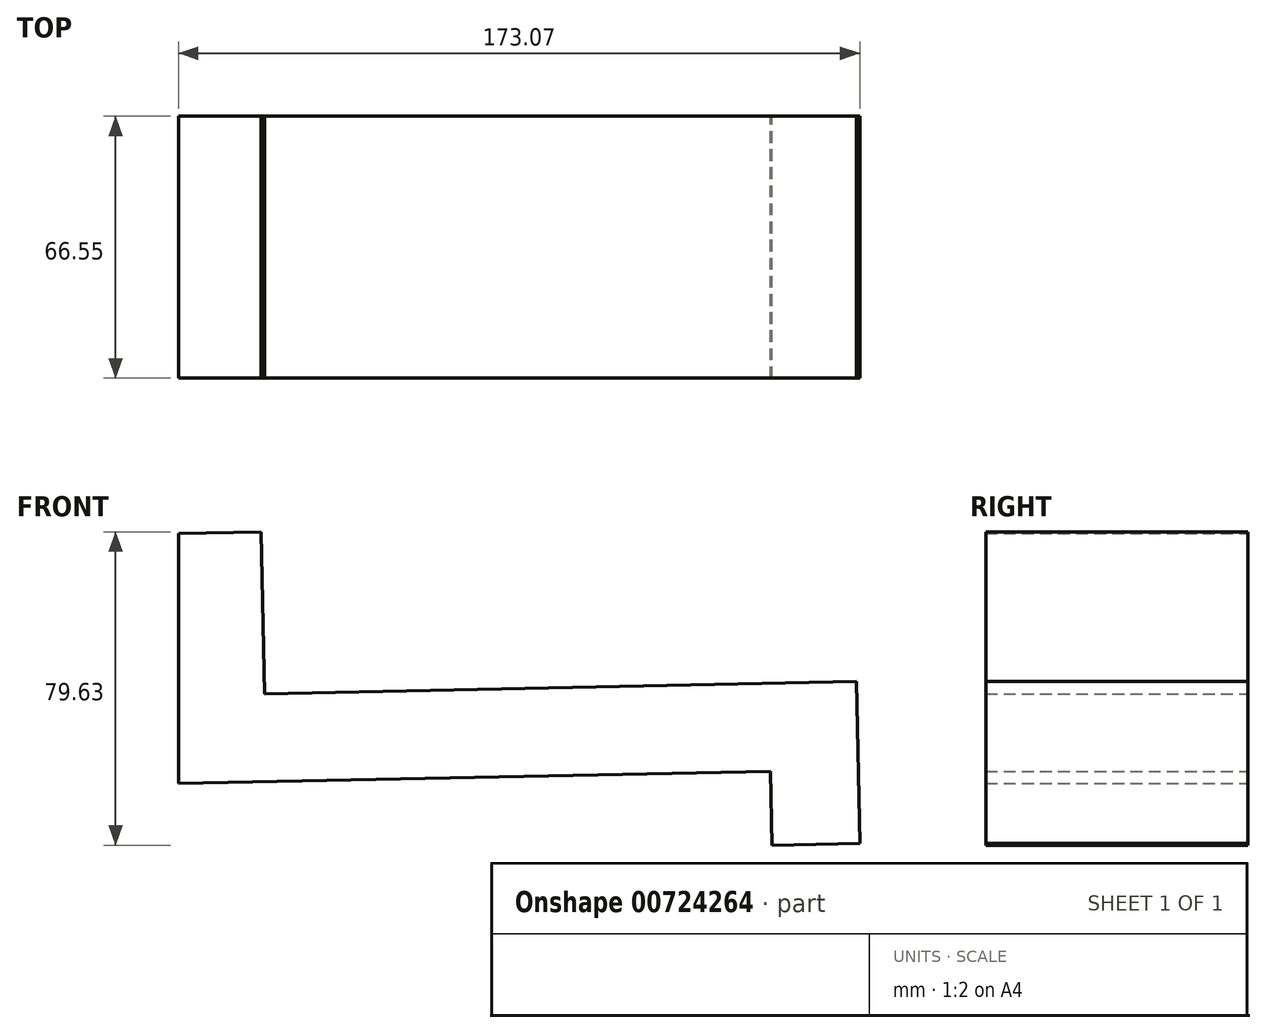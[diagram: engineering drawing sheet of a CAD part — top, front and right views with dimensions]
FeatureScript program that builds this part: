
annotation { "Feature Type Name" : "Feature", "Feature Type Description" : "" }
export const myFeature = defineFeature(function(context is Context, id is Id, definition is map)
    precondition{}
    {
        {
            var Q0;
            Q0=qCreatedBy(makeId("Front.planeOp"),FACE);
            var sketch = newSketch(context, id + "F0", { "sketchPlane" : qUnion([Q0])});
            skLineSegment(sketch, "E0", {"start": v(-93.38, 55.95) * mm, "end": v(-93.38, -7.55) * mm});
            skLineSegment(sketch, "E1", {"start": v(-93.38, -7.55) * mm, "end": v(56.95, -4.44) * mm});
            skLineSegment(sketch, "E2", {"start": v(56.95, -4.44) * mm, "end": v(57.34, -23.23) * mm});
            skLineSegment(sketch, "E3", {"start": v(57.34, -23.23) * mm, "end": v(79.7, -22.77) * mm});
            skLineSegment(sketch, "E4", {"start": v(79.7, -22.77) * mm, "end": v(78.84, 18.37) * mm});
            skLineSegment(sketch, "E5", {"start": v(78.84, 18.37) * mm, "end": v(-71.5, 15.26) * mm});
            skLineSegment(sketch, "E6", {"start": v(-71.5, 15.26) * mm, "end": v(-72.35, 56.4) * mm});
            skLineSegment(sketch, "E7", {"start": v(-72.35, 56.4) * mm, "end": v(-93.38, 55.95) * mm});
            skSolve(sketch);
        }
        {
            var Q0;
            Q0=makeQuery(id+"F0.imprint","IMPRINT",FACE,{"disambiguationData":[TD([[makeQuery(id+"F0.imprint","IMPRINT",EDGE,{"derivedFrom":sQuery(id+"F0.wireOp",EDGE,"E0")}),1.0]])]});
            extrude(context, id + "F1", {"entities" : qUnion([Q0]), "depth" : 66.55 * mm, "offsetDistance" : 25.4 * mm});
        }
    });
